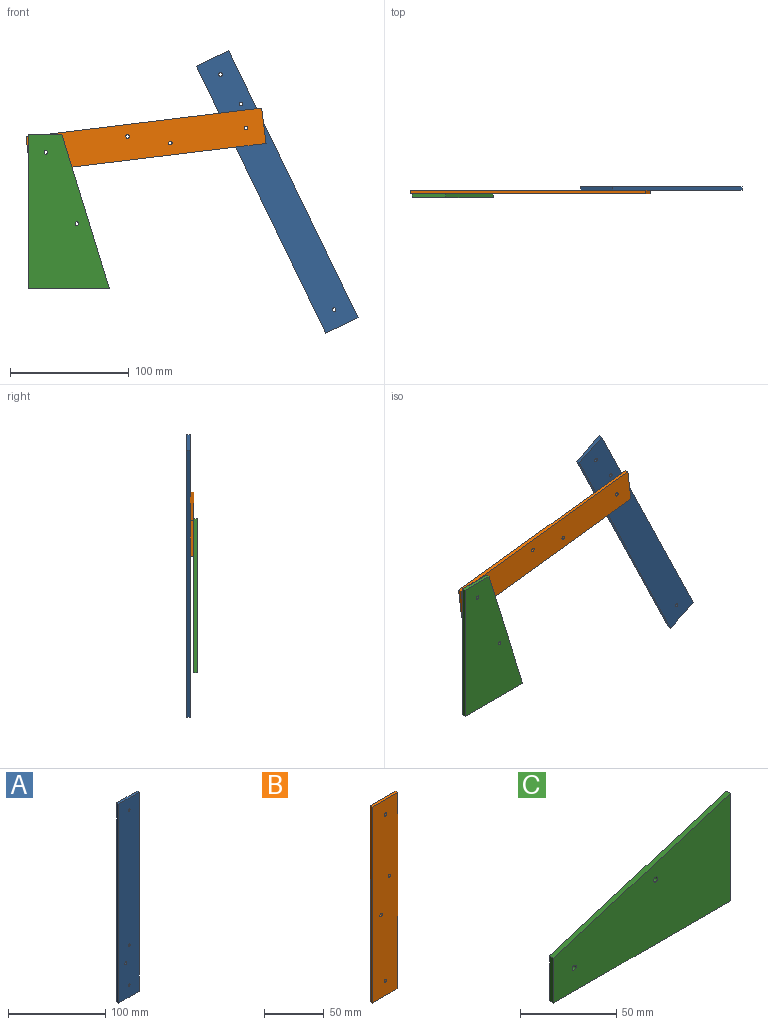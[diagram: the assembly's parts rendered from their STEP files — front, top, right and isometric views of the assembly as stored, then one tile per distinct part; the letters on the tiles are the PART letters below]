
ASSEMBLY  parts=3 mates=2
PART A: 10 faces, bbox 30x3x250 mm
  f0: plane 30x3mm, normal (0,0,-1), area 90mm2, adj f1,f7,f8,f9
  f1: plane 250x3mm, normal (1,0,0), area 750mm2, adj f0,f2,f8,f9
  f2: plane 30x3mm, normal (0,0,1), area 90mm2, adj f1,f7,f8,f9
  f3: cylinder r=1.5mm len=3mm, axis (0,1,0), area 28.3mm2, adj f8,f9
  f4: cylinder r=1.5mm len=3mm, axis (0,1,0), area 28.3mm2, adj f8,f9
  f5: cylinder r=1.5mm len=3mm, axis (0,1,0), area 28.3mm2, adj f8,f9
  f6: cylinder r=1.5mm len=3mm, axis (0,1,0), area 28.3mm2, adj f8,f9
  f7: plane 250x3mm, normal (-1,0,0), area 750mm2, adj f0,f2,f8,f9
  f8: plane 250x30mm, normal (0,-1,0), area 7471.7mm2, adj f0,f1,f2,f3,f4,f5,f6,f7
  f9: plane 250x30mm, normal (0,1,0), area 7471.7mm2, adj f0,f1,f2,f3,f4,f5,f6,f7
PART B: 10 faces, bbox 30x3x200 mm
  f0: plane 200x3mm, normal (1,0,0), area 600mm2, adj f1,f7,f8,f9
  f1: plane 30x3mm, normal (0,0,1), area 90mm2, adj f0,f2,f8,f9
  f2: plane 200x3mm, normal (-1,0,0), area 600mm2, adj f1,f7,f8,f9
  f3: cylinder r=1.5mm len=3mm, axis (0,1,0), area 28.3mm2, adj f8,f9
  f4: cylinder r=1.5mm len=3mm, axis (0,1,0), area 28.3mm2, adj f8,f9
  f5: cylinder r=1.5mm len=3mm, axis (0,1,0), area 28.3mm2, adj f8,f9
  f6: cylinder r=1.5mm len=3mm, axis (0,1,0), area 28.3mm2, adj f8,f9
  f7: plane 30x3mm, normal (0,0,-1), area 90mm2, adj f0,f2,f8,f9
  f8: plane 200x30mm, normal (0,-1,0), area 5971.7mm2, adj f0,f1,f2,f3,f4,f5,f6,f7
  f9: plane 200x30mm, normal (0,1,0), area 5971.7mm2, adj f0,f1,f2,f3,f4,f5,f6,f7
PART C: 8 faces, bbox 130x3x68.5 mm
  f0: plane 68.5x3mm, normal (1,0,0), area 205.5mm2, adj f1,f5,f6,f7
  f1: plane 130x40mm, normal (-0.29,0,0.96), area 408mm2, adj f0,f2,f6,f7
  f2: plane 28.5x3mm, normal (-1,0,0), area 85.5mm2, adj f1,f5,f6,f7
  f3: cylinder r=1.5mm len=3mm, axis (0,1,0), area 28.3mm2, adj f6,f7
  f4: cylinder r=1.5mm len=3mm, axis (0,1,0), area 28.3mm2, adj f6,f7
  f5: plane 130x3mm, normal (0,0,-1), area 390mm2, adj f0,f2,f6,f7
  f6: plane 130x68.5mm, normal (0,-1,0), area 6290.9mm2, adj f0,f1,f2,f3,f4,f5
  f7: plane 130x68.5mm, normal (0,1,0), area 6290.9mm2, adj f0,f1,f2,f3,f4,f5
PLACE A rot(axis=(0,1,0),154.2deg) t=(137.66,18.25,4.7)mm
PLACE B rot(axis=(0,1,0),83deg) t=(73.88,15.25,30.82)mm
PLACE C rot(axis=(0,1,0),90deg) t=(167.51,12.25,26.17)mm fixed
MATE revolute B.f4 <-> C.f4  axis (0,-1,0) through (34.01,12.25,56.17)mm
MATE revolute A.f5 <-> B.f3  axis (0,-1,0) through (202.75,15.25,76.78)mm
